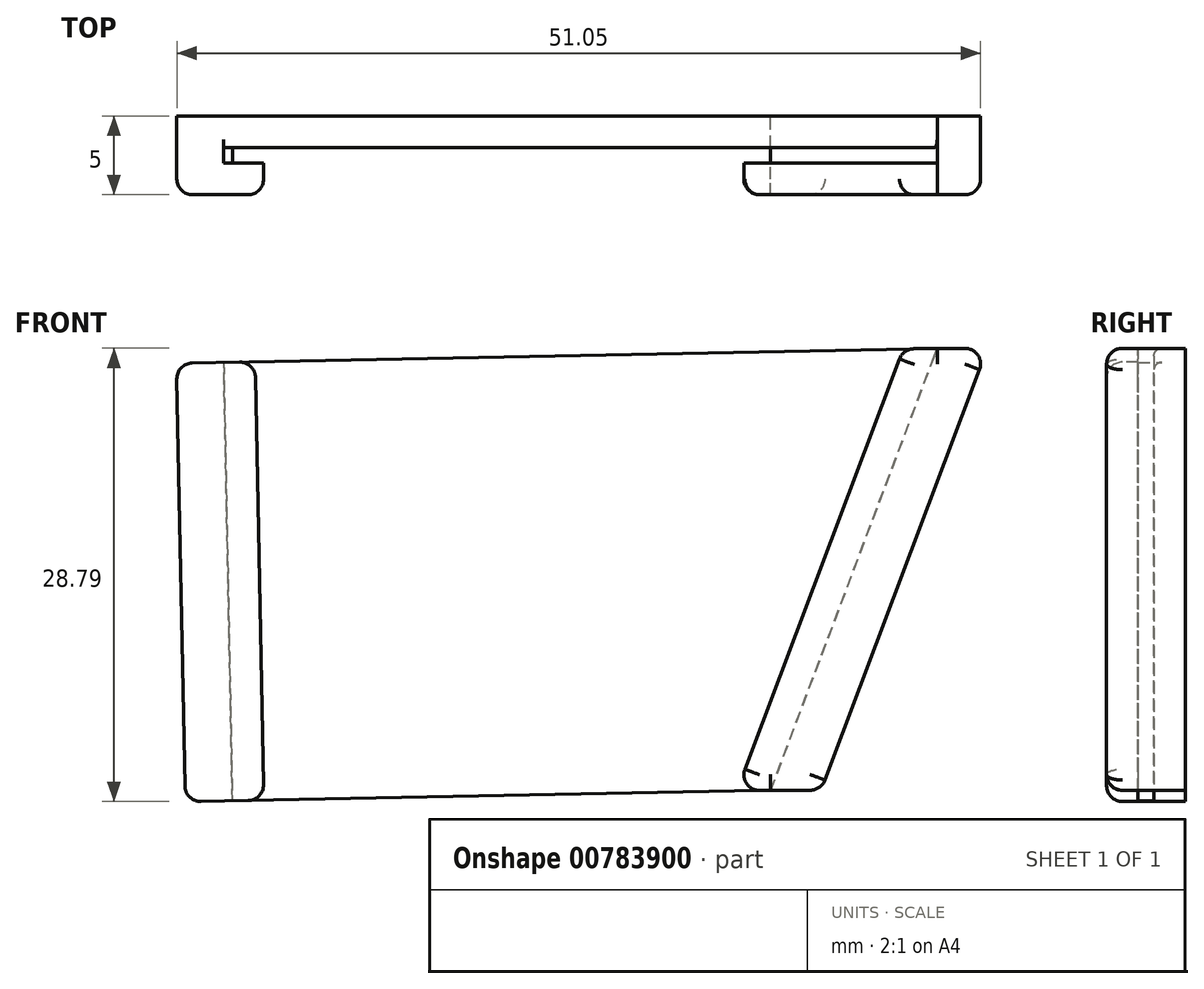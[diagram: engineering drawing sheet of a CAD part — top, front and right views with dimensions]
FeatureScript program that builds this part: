
annotation { "Feature Type Name" : "Feature", "Feature Type Description" : "" }
export const myFeature = defineFeature(function(context is Context, id is Id, definition is map)
    precondition{}
    {
        {
            var Q0;
            Q0=qCreatedBy(makeId("Front.planeOp"),FACE);
            var sketch = newSketch(context, id + "F0", { "sketchPlane" : qUnion([Q0])});
            skLineSegment(sketch, "E0", {"start": v(-28.02, -20) * mm, "end": v(-28.02, 0) * mm});
            skLineSegment(sketch, "E1", {"start": v(-28.02, 0) * mm, "end": v(-33.02, 0) * mm});
            skLineSegment(sketch, "E2", {"start": v(-33.02, 0) * mm, "end": v(-33.02, -20) * mm});
            skLineSegment(sketch, "E3", {"start": v(-33.02, -20) * mm, "end": v(-28.02, -20) * mm});
            skLineSegment(sketch, "E4", {"start": v(-8.39, -20) * mm, "end": v(-0.9, 0) * mm});
            skLineSegment(sketch, "E5", {"start": v(-0.9, 0) * mm, "end": v(4.1, 0) * mm});
            skLineSegment(sketch, "E6", {"start": v(4.1, 0) * mm, "end": v(-3.39, -20) * mm});
            skLineSegment(sketch, "E7", {"start": v(-3.39, -20) * mm, "end": v(-8.39, -20) * mm});
            skLineSegment(sketch, "E8", {"start": v(-33.02, 0) * mm, "end": v(4.1, 0) * mm});
            skLineSegment(sketch, "E9", {"start": v(-30.52, 0) * mm, "end": v(-30.52, -20) * mm});
            skLineSegment(sketch, "E10", {"start": v(1.6, 0) * mm, "end": v(-5.89, -20) * mm});
            skLineSegment(sketch, "E11", {"start": v(-33.72, -20) * mm, "end": v(-3.39, -20) * mm});
            skSolve(sketch);
        }
        {
            var Q0;
            Q0=qCreatedBy(makeId("Front.planeOp"),FACE);
            var sketch = newSketch(context, id + "F1", { "sketchPlane" : qUnion([Q0])});
            skLineSegment(sketch, "E12", {"start": v(-32.07, -10.55) * mm, "end": v(2.1, -9.88) * mm});
            skLineSegment(sketch, "E13", {"start": v(2.1, -9.88) * mm, "end": v(12.69, 18.2) * mm});
            skLineSegment(sketch, "E14", {"start": v(12.69, 18.2) * mm, "end": v(-32.62, 17.3) * mm});
            skLineSegment(sketch, "E15", {"start": v(-32.62, 17.3) * mm, "end": v(-32.07, -10.55) * mm});
            skLineSegment(sketch, "E16", {"start": v(5.31, -9.88) * mm, "end": v(15.9, 18.2) * mm});
            skLineSegment(sketch, "E17", {"start": v(12.69, 18.2) * mm, "end": v(15.9, 18.2) * mm});
            skLineSegment(sketch, "E18", {"start": v(2.1, -9.88) * mm, "end": v(5.31, -9.88) * mm});
            skLineSegment(sketch, "E19.0", {"start": v(-35.62, 17.24) * mm, "end": v(-35.07, -10.61) * mm});
            skLineSegment(sketch, "E20", {"start": v(-32.62, 17.3) * mm, "end": v(-35.62, 17.24) * mm});
            skLineSegment(sketch, "E21", {"start": v(-32.07, -10.55) * mm, "end": v(-35.07, -10.61) * mm});
            skSolve(sketch);
        }
        {
            var Q0;
            Q0 = qSketchRegion(id + "F1", true);
            extrude(context, id + "F2", {"entities" : qUnion([Q0]), "depth" : 2 * mm, "offsetDistance" : 25 * mm});
        }
        {
            var Q0;
            Q0=qCreatedBy(makeId("Front.planeOp"),FACE);
            var sketch = newSketch(context, id + "F3", { "sketchPlane" : qUnion([Q0])});
            skLineSegment(sketch, "E22.0.0", {"start": v(15.9, 18.2) * mm, "end": v(12.69, 18.2) * mm});
            skLineSegment(sketch, "E22.0.1", {"start": v(12.69, 18.2) * mm, "end": v(-35.62, 17.24) * mm});
            skLineSegment(sketch, "E22.0.2", {"start": v(-35.62, 17.24) * mm, "end": v(-35.07, -10.61) * mm});
            skLineSegment(sketch, "E22.0.3", {"start": v(-35.07, -10.61) * mm, "end": v(2.1, -9.88) * mm});
            skLineSegment(sketch, "E22.0.4", {"start": v(2.1, -9.88) * mm, "end": v(5.31, -9.88) * mm});
            skLineSegment(sketch, "E22.0.5", {"start": v(5.31, -9.88) * mm, "end": v(15.9, 18.2) * mm});
            skLineSegment(sketch, "E23", {"start": v(-32.62, 17.3) * mm, "end": v(-32.07, -10.55) * mm});
            skLineSegment(sketch, "E24", {"start": v(12.69, 18.2) * mm, "end": v(2.1, -9.88) * mm});
            skSolve(sketch);
        }
        {
            var Q0;
            Q0=makeQuery(id+"F1.imprint","IMPRINT",FACE,{"disambiguationData":[TD([[makeQuery(id+"F1.imprint","IMPRINT",EDGE,{"derivedFrom":sQuery(id+"F1.wireOp",EDGE,"E15")}),-1.0]])]});
            var Q1;
            Q1=makeQuery(id+"F1.imprint","IMPRINT",FACE,{"disambiguationData":[TD([[makeQuery(id+"F1.imprint","IMPRINT",EDGE,{"derivedFrom":sQuery(id+"F1.wireOp",EDGE,"E13")}),-1.0]])]});
            extrude(context, id + "F4", {"entities" : qUnion([Q0, Q1]), "operationType" : NewBodyOperationType.ADD, "depth" : 5 * mm, "offsetDistance" : 25 * mm});
        }
        {
            var Q0;
            Q0=makeQuery(id+"F4.opExtrude","CAP_FACE",FACE,{"disambiguationData":[OSD([sQuery(id+"F1.wireOp",EDGE,"E15"),sQuery(id+"F1.wireOp",EDGE,"E19.0"),sQuery(id+"F1.wireOp",EDGE,"E20"),sQuery(id+"F1.wireOp",EDGE,"E21")])],"isStart":false});
            var sketch = newSketch(context, id + "F5", { "sketchPlane" : qUnion([Q0])});
            skLineSegment(sketch, "E25.0", {"start": v(-30.62, 17.34) * mm, "end": v(-30.07, -10.51) * mm});
            skLineSegment(sketch, "E26", {"start": v(-30.62, 17.34) * mm, "end": v(-35.62, 17.24) * mm});
            skLineSegment(sketch, "E27", {"start": v(-35.62, 17.24) * mm, "end": v(-35.07, -10.61) * mm});
            skLineSegment(sketch, "E28", {"start": v(-35.07, -10.61) * mm, "end": v(-30.07, -10.51) * mm});
            skLineSegment(sketch, "E29", {"start": v(-0.05, -9.92) * mm, "end": v(2.1, -9.88) * mm});
            skLineSegment(sketch, "E30", {"start": v(5.31, -9.88) * mm, "end": v(2.1, -9.88) * mm});
            skLineSegment(sketch, "E31", {"start": v(5.31, -9.88) * mm, "end": v(15.9, 18.2) * mm});
            skLineSegment(sketch, "E32", {"start": v(15.9, 18.2) * mm, "end": v(12.69, 18.2) * mm});
            skLineSegment(sketch, "E33", {"start": v(12.69, 18.2) * mm, "end": v(10.54, 18.15) * mm});
            skLineSegment(sketch, "E34", {"start": v(-0.05, -9.92) * mm, "end": v(10.54, 18.15) * mm});
            skSolve(sketch);
        }
        {
            var Q0;
            Q0 = qSketchRegion(id + "F5", true);
            extrude(context, id + "F6", {"entities" : qUnion([Q0]), "operationType" : NewBodyOperationType.ADD, "depth" : -2 * mm, "offsetDistance" : 25 * mm});
        }
        {
            var Q0;
            Q0=makeQuery(id+"F4.opExtrude","CAP_EDGE",EDGE,{"disambiguationData":[OSD([sQuery(id+"F1.wireOp",EDGE,"E19.0")])],"isStart":false});
            var Q1;
            Q1=makeQuery(id+"F6.opExtrude","CAP_EDGE",EDGE,{"disambiguationData":[OSD([sQuery(id+"F5.wireOp",EDGE,"E25.0")])],"isStart":true});
            var Q2;
            Q2=makeQuery(id+"F6.opExtrude","CAP_EDGE",EDGE,{"disambiguationData":[OSD([sQuery(id+"F5.wireOp",EDGE,"E34")])],"isStart":true});
            var Q3;
            Q3=makeQuery(id+"F4.opExtrude","CAP_EDGE",EDGE,{"disambiguationData":[OSD([sQuery(id+"F1.wireOp",EDGE,"E16")])],"isStart":false});
            fillet(context, id + "F7", {"entities" : qUnion([Q0, Q1, Q2, Q3]), "tangentPropagation" : true, "radius" : 1 * mm, "defaultsChanged" : true, "vertexSettings" : [], "allowEdgeOverflow" : false});
        }
        {
            var Q0;
            Q0=makeQuery(id+"F2.opExtrude","CAP_EDGE",EDGE,{"disambiguationData":[OSD([sQuery(id+"F1.wireOp",EDGE,"E14"),sQuery(id+"F1.wireOp",EDGE,"E20")])],"isStart":false});
            fillet(context, id + "F8", {"entities" : qUnion([Q0]), "tangentPropagation" : true, "radius" : 0.5 * mm, "defaultsChanged" : true, "vertexSettings" : [], "allowEdgeOverflow" : false});
        }
        {
            var Q0;
            Q0=makeQuery(id+"F6.opExtrude","SWEPT_EDGE",EDGE,{"disambiguationData":[OSD([sQuery(id+"F5.wireOp",EDGE,"E25.0"),sQuery(id+"F5.wireOp",EDGE,"E26")])]});
            var Q1;
            Q1=makeQuery(id+"F6.opExtrude","SWEPT_EDGE",EDGE,{"disambiguationData":[OSD([sQuery(id+"F5.wireOp",EDGE,"E33"),sQuery(id+"F5.wireOp",EDGE,"E34")])]});
            var Q2;
            {var subQ0=sQuery(id+"F1.wireOp",EDGE,"E17");var subQ1=sQuery(id+"F1.wireOp",EDGE,"E16");Q2=makeQuery(id+"F4.boolean.opBoolean","MERGE",EDGE,{"derivedFrom":[makeQuery(id+"F2.opExtrude","SWEPT_EDGE",EDGE,{"disambiguationData":[OSD([subQ1,subQ0])]}),makeQuery(id+"F4.opExtrude","SWEPT_EDGE",EDGE,{"disambiguationData":[OSD([subQ1,subQ0])]})]});}
            fillet(context, id + "F9", {"entities" : qUnion([Q0, Q1, Q2]), "tangentPropagation" : true, "radius" : 1 * mm, "defaultsChanged" : false, "vertexSettings" : [], "allowEdgeOverflow" : false});
        }
        {
            var Q0;
            {var subQ0=sQuery(id+"F1.wireOp",EDGE,"E21");var subQ1=sQuery(id+"F1.wireOp",EDGE,"E19.0");Q0=makeQuery(id+"F4.boolean.opBoolean","MERGE",EDGE,{"derivedFrom":[makeQuery(id+"F2.opExtrude","SWEPT_EDGE",EDGE,{"disambiguationData":[OSD([subQ1,subQ0])]}),makeQuery(id+"F4.opExtrude","SWEPT_EDGE",EDGE,{"disambiguationData":[OSD([subQ1,subQ0])]})]});}
            var Q1;
            {var subQ0=sQuery(id+"F1.wireOp",EDGE,"E18");var subQ1=sQuery(id+"F1.wireOp",EDGE,"E16");Q1=makeQuery(id+"F6.boolean.opBoolean","SPLIT",EDGE,{"disambiguationData":[TD([makeQuery(id+"F2.opExtrude","CAP_FACE",FACE,{"disambiguationData":[OSD([sQuery(id+"F1.wireOp",EDGE,"E12"),sQuery(id+"F1.wireOp",EDGE,"E14"),subQ1,sQuery(id+"F1.wireOp",EDGE,"E17"),subQ0,sQuery(id+"F1.wireOp",EDGE,"E19.0"),sQuery(id+"F1.wireOp",EDGE,"E20"),sQuery(id+"F1.wireOp",EDGE,"E21")])],"isStart":true})])],"derivedFrom":makeQuery(id+"F4.boolean.opBoolean","MERGE",EDGE,{"derivedFrom":[makeQuery(id+"F2.opExtrude","SWEPT_EDGE",EDGE,{"disambiguationData":[OSD([subQ1,subQ0])]}),makeQuery(id+"F4.opExtrude","SWEPT_EDGE",EDGE,{"disambiguationData":[OSD([subQ1,subQ0])]})]})});}
            var Q2;
            {var subQ0=sQuery(id+"F1.wireOp",EDGE,"E18");var subQ1=sQuery(id+"F1.wireOp",EDGE,"E16");Q2=makeQuery(id+"F6.boolean.opBoolean","SPLIT",EDGE,{"disambiguationData":[TD([makeQuery(id+"F4.opExtrude","CAP_FACE",FACE,{"disambiguationData":[OSD([sQuery(id+"F1.wireOp",EDGE,"E13"),subQ1,sQuery(id+"F1.wireOp",EDGE,"E17"),subQ0])],"isStart":false})])],"derivedFrom":makeQuery(id+"F4.boolean.opBoolean","MERGE",EDGE,{"derivedFrom":[makeQuery(id+"F2.opExtrude","SWEPT_EDGE",EDGE,{"disambiguationData":[OSD([subQ1,subQ0])]}),makeQuery(id+"F4.opExtrude","SWEPT_EDGE",EDGE,{"disambiguationData":[OSD([subQ1,subQ0])]})]})});}
            var Q3;
            Q3=makeQuery(id+"F6.opExtrude","SWEPT_EDGE",EDGE,{"disambiguationData":[OSD([sQuery(id+"F5.wireOp",EDGE,"E29"),sQuery(id+"F5.wireOp",EDGE,"E34")])]});
            fillet(context, id + "F10", {"entities" : qUnion([Q0, Q1, Q2, Q3]), "tangentPropagation" : true, "radius" : 1 * mm, "defaultsChanged" : false, "vertexSettings" : [], "allowEdgeOverflow" : false});
        }
    });
